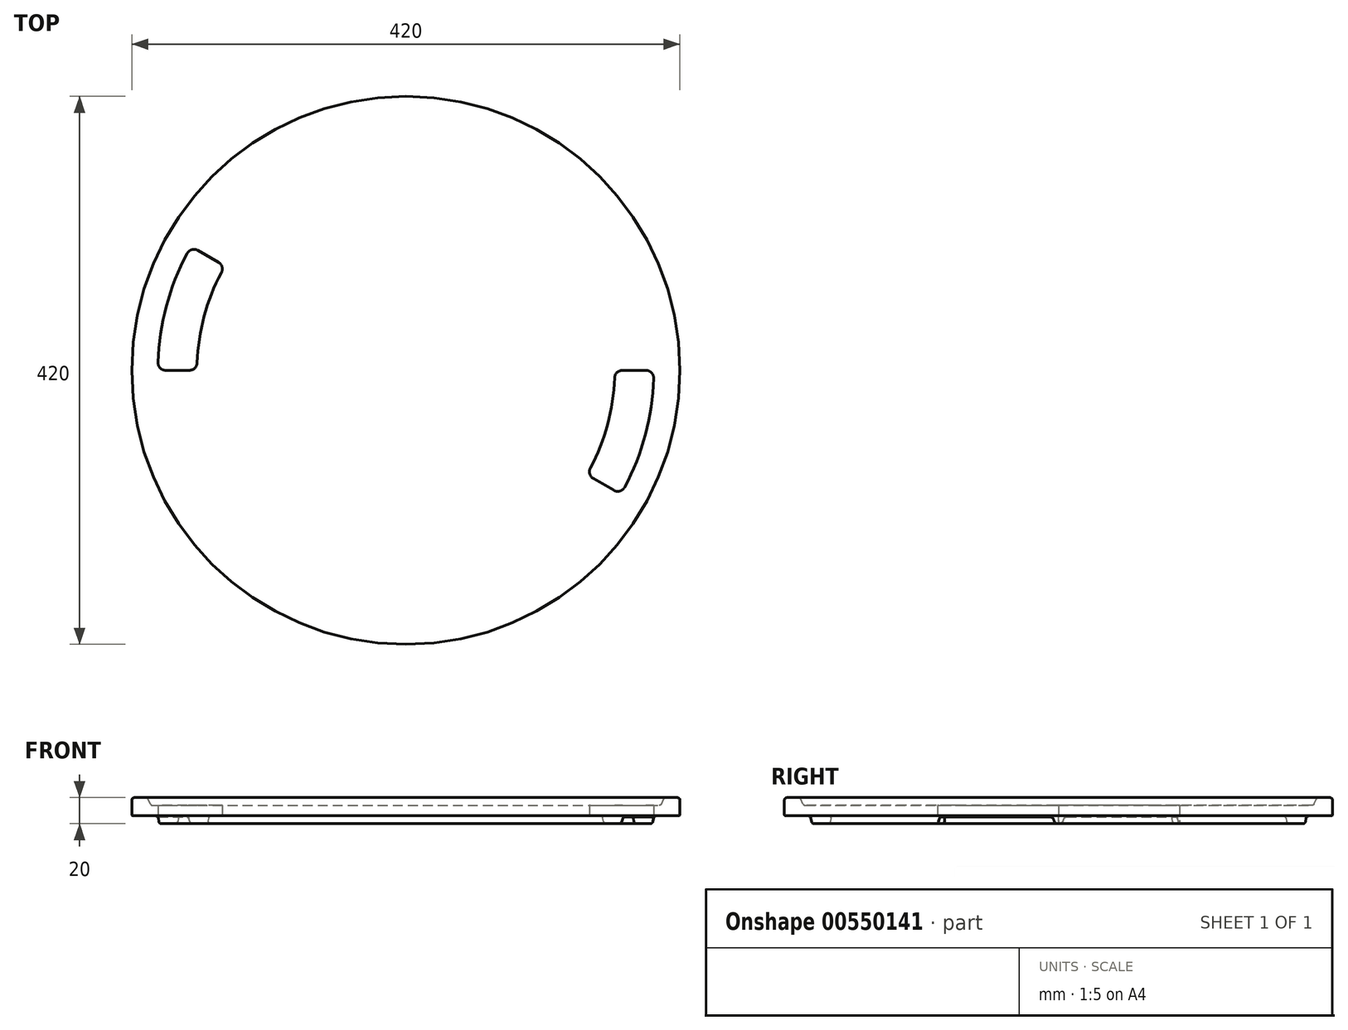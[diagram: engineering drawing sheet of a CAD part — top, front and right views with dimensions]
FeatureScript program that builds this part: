
annotation { "Feature Type Name" : "Feature", "Feature Type Description" : "" }
export const myFeature = defineFeature(function(context is Context, id is Id, definition is map)
    precondition{}
    {
        {
            var Q0;
            Q0=qCreatedBy(makeId("Front.planeOp"),FACE);
            var sketch = newSketch(context, id + "F0", { "sketchPlane" : qUnion([Q0])});
            skLineSegment(sketch, "E0", {"start": v(0, 0) * mm, "end": v(210, 0) * mm, "construction": true});
            skLineSegment(sketch, "E1", {"start": v(193.93, 14) * mm, "end": v(0, 14) * mm});
            skLineSegment(sketch, "E2", {"start": v(0, 14) * mm, "end": v(0, 6) * mm});
            skLineSegment(sketch, "E3", {"start": v(0, 6) * mm, "end": v(172.32, 6) * mm});
            skLineSegment(sketch, "E4", {"start": v(174.3, 4.35) * mm, "end": v(174.77, 1.65) * mm});
            skLineSegment(sketch, "E5", {"start": v(176.74, 0) * mm, "end": v(187.26, 0) * mm});
            skLineSegment(sketch, "E6", {"start": v(189.23, 1.65) * mm, "end": v(189.7, 4.35) * mm});
            skPoint(sketch, "E7.visualSharp", {"position": v(190, 6) * mm});
            skArc(sketch, "E7.filletArc", {"start": v(191.68, 6) * mm, "mid": v(190.4, 5.53) * mm, "end": v(189.7, 4.35) * mm});
            skPoint(sketch, "E8.visualSharp", {"position": v(174, 6) * mm});
            skArc(sketch, "E8.filletArc", {"start": v(174.3, 4.35) * mm, "mid": v(173.6, 5.53) * mm, "end": v(172.32, 6) * mm});
            skPoint(sketch, "E9.visualSharp", {"position": v(188.94, 0) * mm});
            skArc(sketch, "E9.filletArc", {"start": v(187.26, 0) * mm, "mid": v(188.55, 0.47) * mm, "end": v(189.23, 1.65) * mm});
            skPoint(sketch, "E10.visualSharp", {"position": v(175.06, 0) * mm});
            skArc(sketch, "E10.filletArc", {"start": v(174.77, 1.65) * mm, "mid": v(175.45, 0.47) * mm, "end": v(176.74, 0) * mm});
            skLineSegment(sketch, "E11", {"start": v(0, 0) * mm, "end": v(0, 14) * mm, "construction": true});
            skLineSegment(sketch, "E12", {"start": v(191.68, 6) * mm, "end": v(209, 6) * mm});
            skLineSegment(sketch, "E13", {"start": v(210, 7) * mm, "end": v(210, 18) * mm});
            skArc(sketch, "E14.filletArc", {"start": v(209, 6) * mm, "mid": v(209.7, 6.3) * mm, "end": v(210, 7) * mm});
            skLineSegment(sketch, "E15", {"start": v(208, 20) * mm, "end": v(199.27, 20) * mm});
            skLineSegment(sketch, "E16", {"start": v(197.46, 18.85) * mm, "end": v(195.74, 15.15) * mm});
            skPoint(sketch, "E17.visualSharp", {"position": v(195.2, 14) * mm});
            skArc(sketch, "E17.filletArc", {"start": v(193.93, 14) * mm, "mid": v(195, 14.31) * mm, "end": v(195.74, 15.15) * mm});
            skPoint(sketch, "E18.visualSharp", {"position": v(198, 20) * mm});
            skArc(sketch, "E18.filletArc", {"start": v(199.27, 20) * mm, "mid": v(198.2, 19.69) * mm, "end": v(197.46, 18.85) * mm});
            skPoint(sketch, "E19.visualSharp", {"position": v(210, 20) * mm});
            skArc(sketch, "E19.filletArc", {"start": v(210, 18) * mm, "mid": v(209.41, 19.41) * mm, "end": v(208, 20) * mm});
            skSolve(sketch);
        }
        {
            var Q0;
            Q0=makeQuery(id+"F0.imprint","IMPRINT",FACE,{"disambiguationData":[TD([[makeQuery(id+"F0.imprint","IMPRINT",EDGE,{"derivedFrom":sQuery(id+"F0.wireOp",EDGE,"E1")}),1.0]])]});
            var Q1;
            Q1=sQuery(id+"F0.wireOp",EDGE,"E11");
            revolve(context, id + "F1", {"entities" : qUnion([Q0]), "axis" : qUnion([Q1]), "revolveType" : RevolveType.FULL});
        }
        {
            var Q0;
            Q0=qCreatedBy(makeId("Top.planeOp"),FACE);
            var sketch = newSketch(context, id + "F2", { "sketchPlane" : qUnion([Q0])});
            skCircle(sketch, "E20", {"center": v(0, 0) * mm, "radius": 190 * mm, "construction": true});
            skLineSegment(sketch, "E21", {"start": v(190, 0) * mm, "end": v(-190, 0) * mm, "construction": true});
            skLineSegment(sketch, "E22", {"start": v(0, 190) * mm, "end": v(0, -190) * mm, "construction": true});
            skArc(sketch, "E23", {"start": v(-189.9, 6.2) * mm, "mid": v(-183.53, 49.18) * mm, "end": v(-167.56, 89.58) * mm});
            skArc(sketch, "E24", {"start": v(-159.9, 5.78) * mm, "mid": v(-154.55, 41.41) * mm, "end": v(-141.37, 74.94) * mm});
            skLineSegment(sketch, "E25", {"start": v(-165.9, 0) * mm, "end": v(-183.9, 0) * mm});
            skLineSegment(sketch, "E26", {"start": v(164.54, -95) * mm, "end": v(-164.54, 95) * mm, "construction": true});
            skLineSegment(sketch, "E27", {"start": v(-159.26, 91.95) * mm, "end": v(-143.67, 82.95) * mm});
            skArc(sketch, "E28", {"start": v(159.9, -5.78) * mm, "mid": v(154.55, -41.41) * mm, "end": v(141.37, -74.94) * mm});
            skArc(sketch, "E29", {"start": v(189.9, -6.2) * mm, "mid": v(183.53, -49.18) * mm, "end": v(167.56, -89.58) * mm});
            skLineSegment(sketch, "E30", {"start": v(183.9, 0) * mm, "end": v(165.9, 0) * mm});
            skLineSegment(sketch, "E31", {"start": v(159.26, -91.95) * mm, "end": v(143.67, -82.95) * mm});
            skPoint(sketch, "E32.visualSharp", {"position": v(-164.54, 95) * mm});
            skArc(sketch, "E32.filletArc", {"start": v(-159.26, 91.95) * mm, "mid": v(-163.91, 92.52) * mm, "end": v(-167.56, 89.58) * mm});
            skPoint(sketch, "E33.visualSharp", {"position": v(-138.56, 80) * mm});
            skArc(sketch, "E33.filletArc", {"start": v(-141.37, 74.94) * mm, "mid": v(-140.9, 79.4) * mm, "end": v(-143.67, 82.95) * mm});
            skPoint(sketch, "E34.visualSharp", {"position": v(-160, 0) * mm});
            skArc(sketch, "E34.filletArc", {"start": v(-165.9, 0) * mm, "mid": v(-161.73, 1.68) * mm, "end": v(-159.9, 5.78) * mm});
            skPoint(sketch, "E35.visualSharp", {"position": v(-190, 0) * mm});
            skArc(sketch, "E35.filletArc", {"start": v(-189.9, 6.2) * mm, "mid": v(-188.21, 1.83) * mm, "end": v(-183.9, 0) * mm});
            skPoint(sketch, "E36.visualSharp", {"position": v(190, 0) * mm});
            skArc(sketch, "E36.filletArc", {"start": v(189.9, -6.2) * mm, "mid": v(188.21, -1.83) * mm, "end": v(183.9, 0) * mm});
            skPoint(sketch, "E37.visualSharp", {"position": v(160, 0) * mm});
            skArc(sketch, "E37.filletArc", {"start": v(165.9, 0) * mm, "mid": v(161.73, -1.68) * mm, "end": v(159.9, -5.78) * mm});
            skPoint(sketch, "E38.visualSharp", {"position": v(138.56, -80) * mm});
            skArc(sketch, "E38.filletArc", {"start": v(141.37, -74.94) * mm, "mid": v(140.9, -79.4) * mm, "end": v(143.67, -82.95) * mm});
            skPoint(sketch, "E39.visualSharp", {"position": v(164.54, -95) * mm});
            skArc(sketch, "E39.filletArc", {"start": v(159.26, -91.95) * mm, "mid": v(163.91, -92.52) * mm, "end": v(167.56, -89.58) * mm});
            skSolve(sketch);
        }
        {
            var Q0;
            Q0 = qSketchRegion(id + "F2", true);
            extrude(context, id + "F3", {"entities" : qUnion([Q0]), "operationType" : NewBodyOperationType.REMOVE, "depth" : 25 * mm, "offsetDistance" : 25 * mm});
        }
    });
